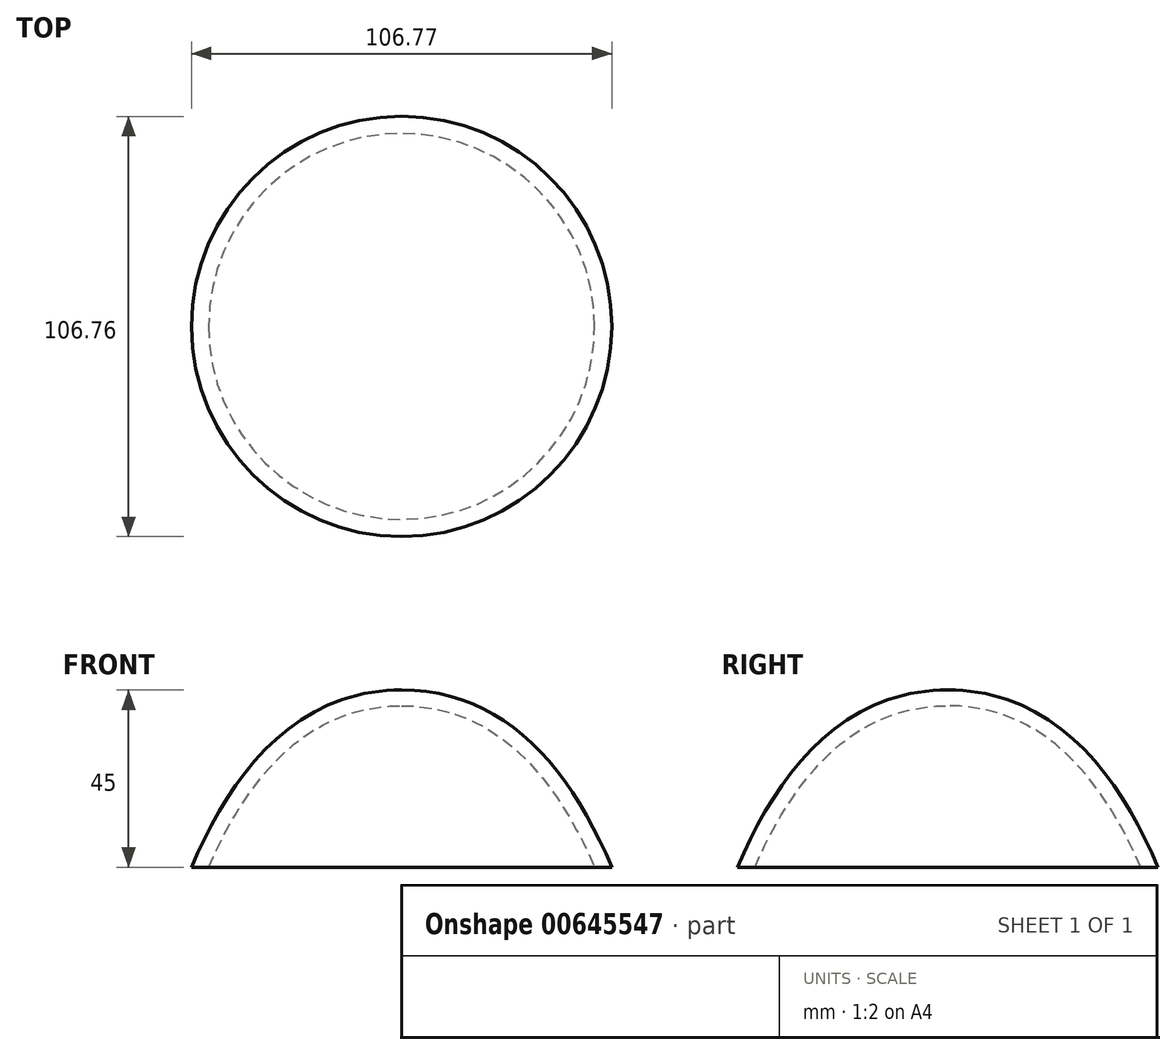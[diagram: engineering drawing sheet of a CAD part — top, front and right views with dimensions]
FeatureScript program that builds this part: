
annotation { "Feature Type Name" : "Feature", "Feature Type Description" : "" }
export const myFeature = defineFeature(function(context is Context, id is Id, definition is map)
    precondition{}
    {
        {
            var Q0;
            Q0=qCreatedBy(makeId("Front.planeOp"),FACE);
            var sketch = newSketch(context, id + "F0", { "sketchPlane" : qUnion([Q0])});
            skLineSegment(sketch, "E0", {"start": v(-26.63, 80.21) * mm, "end": v(-26.63, 125.21) * mm});
            skFitSpline(sketch, "E1", {"points": [v(-26.63, 125.21) * mm, v(48.37, -74.79) * mm], "startDerivative": vector(195.84, 0) * mm, "endDerivative": vector(0, -233.52) * mm});
            skLineSegment(sketch, "E2", {"start": v(-26.63, 125.21) * mm, "end": v(-99.65, 125.21) * mm, "construction": true});
            skLineSegment(sketch, "E3", {"start": v(-26.63, 80.21) * mm, "end": v(26.75, 80.21) * mm});
            skPoint(sketch, "E4.start.orphan", {"position": v(-26.63, -74.79) * mm});
            skSolve(sketch);
        }
        {
            var Q0;
            Q0 = qSketchRegion(id + "F0", true);
            var Q1;
            Q1=sQuery(id+"F0.wireOp",EDGE,"E0");
            revolve(context, id + "F1", {"entities" : qUnion([Q0]), "axis" : qUnion([Q1]), "revolveType" : RevolveType.FULL});
        }
        {
            var Q0;
            Q0=makeQuery(id+"F1.opRevolve","SWEPT_FACE",FACE,{"disambiguationData":[OSD([sQuery(id+"F0.wireOp",EDGE,"E3")])]});
            shell(context, id + "F2", {"entities" : qUnion([Q0]), "thickness" : 4 * mm});
        }
    });
